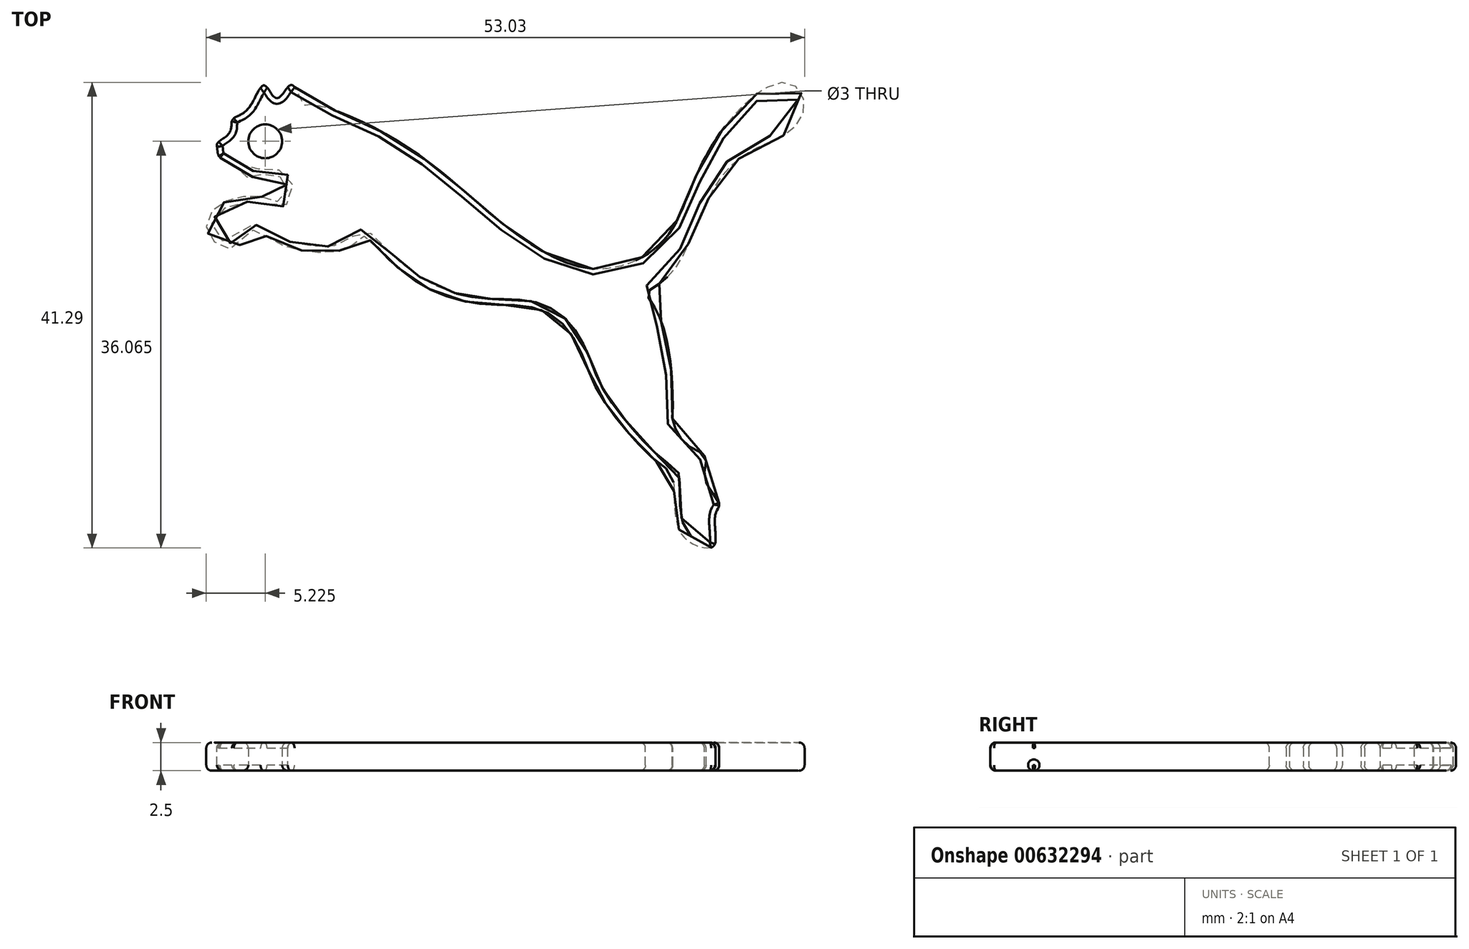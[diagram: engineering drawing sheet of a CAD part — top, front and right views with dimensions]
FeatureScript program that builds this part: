
annotation { "Feature Type Name" : "Feature", "Feature Type Description" : "" }
export const myFeature = defineFeature(function(context is Context, id is Id, definition is map)
    precondition{}
    {
        {
            var Q0;
            Q0=qCreatedBy(makeId("Top.planeOp"),FACE);
            var sketch = newSketch(context, id + "F0", { "sketchPlane" : qUnion([Q0])});
            skFitSpline(sketch, "E0", {"points": [v(-22.79, 9.2) * mm, v(-22.77, 9.67) * mm, v(-21.66, 10.65) * mm, v(-21.43, 11.75) * mm, v(-20.16, 12.6) * mm, v(-18.72, 14.79) * mm, v(-18.07, 14.19) * mm, v(-17.5, 13.66) * mm, v(-16.82, 14.26) * mm, v(-16.13, 14.8) * mm, v(-15.07, 13.06) * mm, v(-14.8, 13.06) * mm, v(-11.97, 12.43) * mm, v(-4.55, 8.37) * mm, v(1.8, 3.1) * mm, v(7.47, -0.64) * mm, v(11.95, -1.43) * mm, v(16.66, 0.93) * mm, v(19.18, 5.65) * mm, v(21.38, 9.97) * mm, v(24.84, 13.9) * mm, v(27.9, 15) * mm, v(29.24, 13.35) * mm, v(28.38, 11.07) * mm, v(25.39, 9.42) * mm, v(22, 6.83) * mm, v(18.94, 0.7) * mm, v(17.6, -1.66) * mm, v(15.48, -3.4) * mm, v(15.17, -3.54) * mm, v(15.87, -4.7) * mm, v(17.28, -9.04) * mm, v(17.56, -14.24) * mm, v(17.56, -14.84) * mm, v(18.53, -16.79) * mm, v(19.97, -17.72) * mm, v(20.53, -18.37) * mm, v(20.44, -20.18) * mm, v(21.7, -22.27) * mm, v(21.37, -23.24) * mm, v(21.37, -25.7) * mm, v(20.86, -26.21) * mm, v(18.77, -25.47) * mm, v(17.75, -22.6) * mm, v(17.51, -19.34) * mm, v(17.05, -19.2) * mm, v(11.52, -13.26) * mm, v(9.76, -9.6) * mm, v(7.95, -6.48) * mm, v(5.02, -4.86) * mm, v(0.57, -4.58) * mm, v(-4.22, -3.14) * mm, v(-7.57, -0.62) * mm, v(-9.22, 1.03) * mm, v(-9.87, 1.48) * mm, v(-10.07, 1.48) * mm, v(-10.82, 0.63) * mm, v(-13.38, 0) * mm, v(-16.98, 0.63) * mm, v(-19.23, 1.84) * mm, v(-20.33, 1.94) * mm, v(-20.58, 1.33) * mm, v(-20.93, 0.48) * mm, v(-22.38, 0.48) * mm, v(-23.74, 2.09) * mm, v(-22.78, 4.09) * mm, v(-18.93, 4.94) * mm, v(-17.38, 4.49) * mm, v(-16.68, 5.04) * mm, v(-16.88, 6.49) * mm, v(-18.98, 6.9) * mm, v(-19.83, 6.64) * mm, v(-20.78, 7.04) * mm, v(-21.53, 7.94) * mm, v(-22.58, 8.44) * mm, v(-22.79, 9.2) * mm]});
            skSolve(sketch);
        }
        {
            var Q0;
            Q0=makeQuery(id+"F0.imprint","IMPRINT",FACE,{"disambiguationData":[TD([[makeQuery(id+"F0.imprint","IMPRINT",EDGE,{"derivedFrom":sQuery(id+"F0.wireOp",EDGE,"E0")}),-1.0]])]});
            extrude(context, id + "F1", {"entities" : qUnion([Q0]), "depth" : 2.5 * mm, "offsetDistance" : 25 * mm});
        }
        {
            var Q0;
            Q0=qCreatedBy(makeId("Top.planeOp"),FACE);
            var sketch = newSketch(context, id + "F2", { "sketchPlane" : qUnion([Q0])});
            skCircle(sketch, "E1", {"center": v(-18.53, 9.84) * mm, "radius": 1.5 * mm});
            skSolve(sketch);
        }
        {
            var Q0;
            Q0=makeQuery(id+"F2.imprint","IMPRINT",FACE,{"disambiguationData":[TD([[makeQuery(id+"F2.imprint","IMPRINT",EDGE,{"derivedFrom":sQuery(id+"F2.wireOp",EDGE,"E1")}),1.0]])]});
            extrude(context, id + "F3", {"entities" : qUnion([Q0]), "operationType" : NewBodyOperationType.REMOVE, "endBound" : BoundingType.THROUGH_ALL, "depth" : 25 * mm, "offsetDistance" : 25 * mm});
        }
        {
            var Q0;
            Q0=makeQuery(id+"F1.opExtrude","CAP_FACE",FACE,{"disambiguationData":[OSD([sQuery(id+"F0.wireOp",EDGE,"E0")])],"isStart":false});
            var Q1;
            Q1=makeQuery(id+"F1.opExtrude","CAP_FACE",FACE,{"disambiguationData":[OSD([sQuery(id+"F0.wireOp",EDGE,"E0")])],"isStart":true});
            fillet(context, id + "F4", {"entities" : qUnion([Q0, Q1]), "radius" : .5 * mm, "tangentPropagation" : true, "allowEdgeOverflow" : false});
        }
    });
